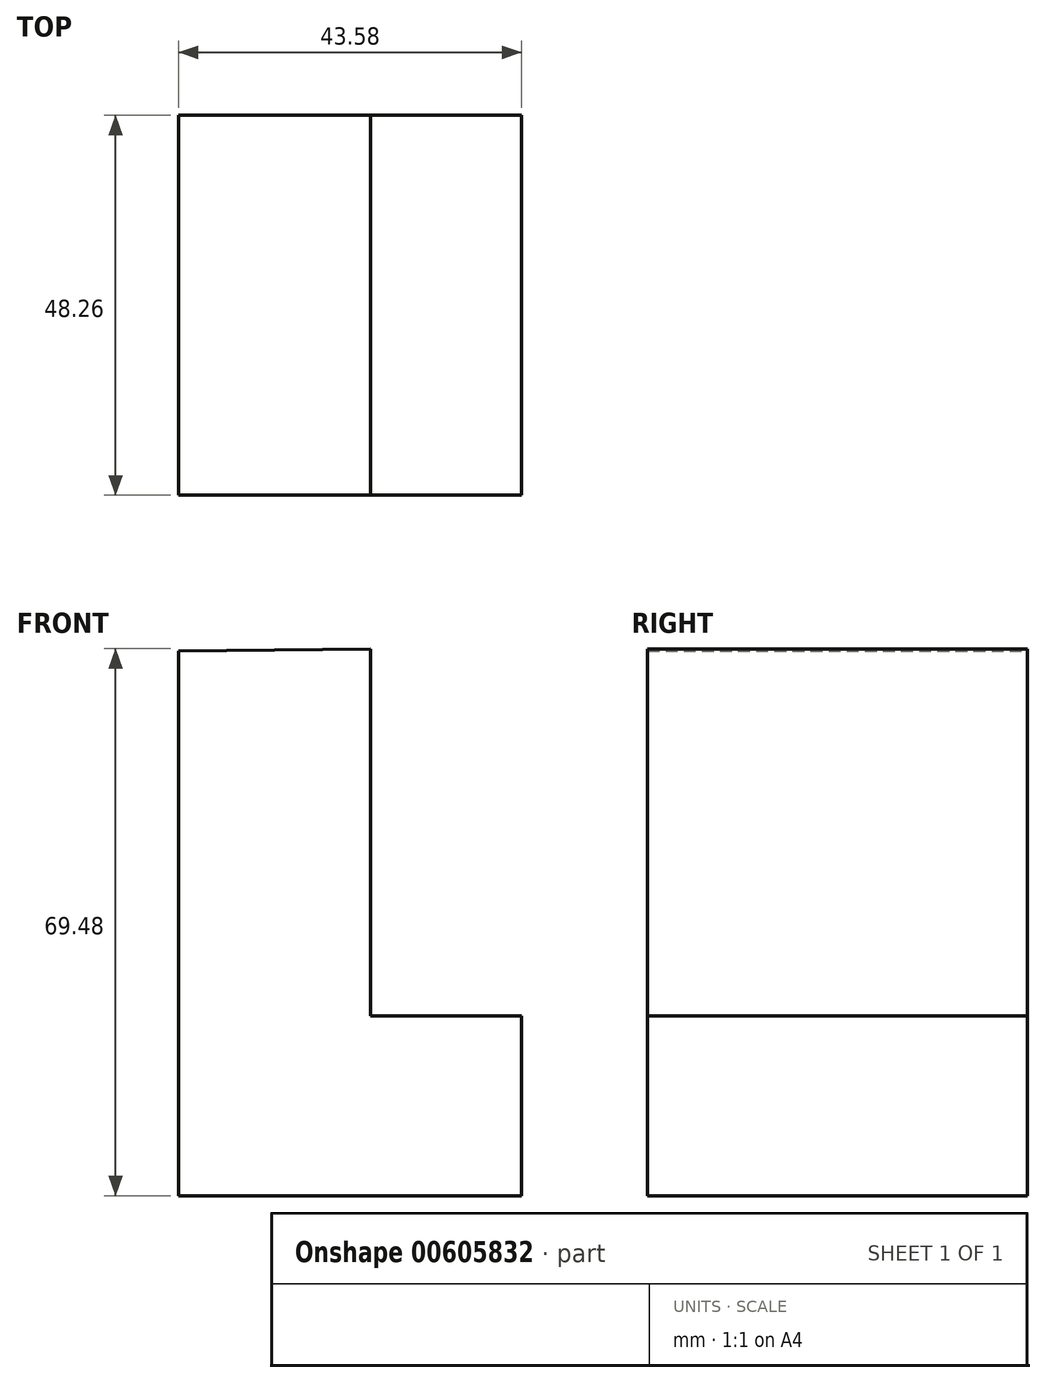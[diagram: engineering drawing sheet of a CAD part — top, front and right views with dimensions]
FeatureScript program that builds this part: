
annotation { "Feature Type Name" : "Feature", "Feature Type Description" : "" }
export const myFeature = defineFeature(function(context is Context, id is Id, definition is map)
    precondition{}
    {
        {
            var Q0;
            Q0=qCreatedBy(makeId("Front.planeOp"),FACE);
            var sketch = newSketch(context, id + "F0", { "sketchPlane" : qUnion([Q0])});
            skLineSegment(sketch, "E0", {"start": v(-38.86, 28.65) * mm, "end": v(-38.86, -40.54) * mm});
            skLineSegment(sketch, "E1", {"start": v(-38.86, -40.54) * mm, "end": v(4.72, -40.54) * mm});
            skLineSegment(sketch, "E2", {"start": v(4.72, -40.54) * mm, "end": v(4.72, -17.68) * mm});
            skLineSegment(sketch, "E3", {"start": v(4.72, -17.68) * mm, "end": v(-14.48, -17.68) * mm});
            skLineSegment(sketch, "E4", {"start": v(-14.48, -17.68) * mm, "end": v(-14.48, 28.94) * mm});
            skLineSegment(sketch, "E5", {"start": v(-14.48, 28.94) * mm, "end": v(-38.86, 28.65) * mm});
            skSolve(sketch);
        }
        {
            var Q0;
            Q0 = qSketchRegion(id + "F0", true);
            extrude(context, id + "F1", {"entities" : qUnion([Q0]), "depth" : 48.26 * mm, "offsetDistance" : 25.4 * mm});
        }
    });
